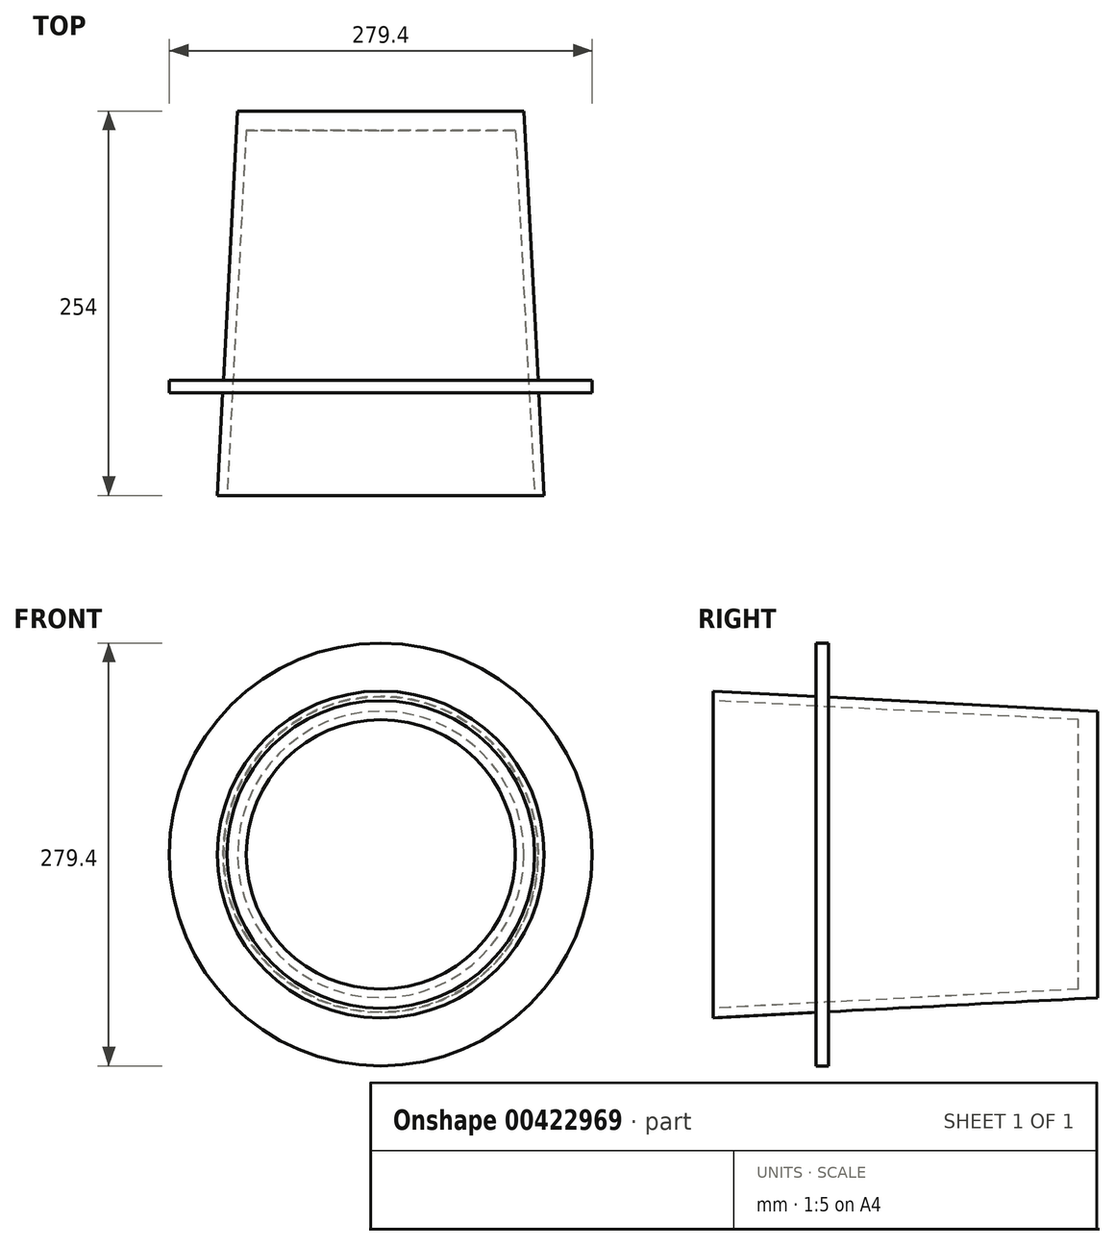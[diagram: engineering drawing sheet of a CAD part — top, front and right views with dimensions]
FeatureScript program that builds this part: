
annotation { "Feature Type Name" : "Feature", "Feature Type Description" : "" }
export const myFeature = defineFeature(function(context is Context, id is Id, definition is map)
    precondition{}
    {
        {
            var Q0;
            Q0=qCreatedBy(makeId("Front.planeOp"),FACE);
            var sketch = newSketch(context, id + "F0", { "sketchPlane" : qUnion([Q0])});
            skCircle(sketch, "E0", {"center": v(0, 0) * mm, "radius": 107.95 * mm});
            skSolve(sketch);
        }
        {
            var Q0;
            Q0 = qSketchRegion(id + "F0", true);
            extrude(context, id + "F1", {"entities" : qUnion([Q0]), "oppositeDirection" : true, "depth" : 254 * mm, "hasDraft" : true, "draftAngle" : 3 * degree, "draftPullDirection" : true});
        }
        {
            var Q0;
            Q0=makeQuery(id+"F1.opExtrude","CAP_FACE",FACE,{"disambiguationData":[OSD([sQuery(id+"F0.wireOp",EDGE,"E0")])],"isStart":true});
            var sketch = newSketch(context, id + "F2", { "sketchPlane" : qUnion([Q0])});
            skCircle(sketch, "E1", {"center": v(0, 0) * mm, "radius": 101.6 * mm});
            skSolve(sketch);
        }
        {
            var Q0;
            Q0 = qSketchRegion(id + "F2", true);
            extrude(context, id + "F3", {"entities" : qUnion([Q0]), "operationType" : NewBodyOperationType.REMOVE, "oppositeDirection" : true, "depth" : 241.3 * mm, "hasDraft" : true, "draftAngle" : 3 * degree, "draftPullDirection" : true});
        }
        {
            var Q0;
            Q0=makeQuery(id+"F1.opExtrude","CAP_FACE",FACE,{"disambiguationData":[OSD([sQuery(id+"F0.wireOp",EDGE,"E0")])],"isStart":true});
            cPlane(context, id + "F4", {"entities" : qUnion([Q0]), "cplaneType" : CPlaneType.OFFSET, "offset" : 76.2 * mm, "oppositeDirection" : true, "width" : 152.4 * mm, "height" : 152.4 * mm});
        }
        {
            var Q0;
            Q0=qCreatedBy(id+"F4.planeOp",FACE);
            var sketch = newSketch(context, id + "F5", { "sketchPlane" : qUnion([Q0])});
            skArc(sketch, "E2", {"start": v(-103.95, 0) * mm, "mid": v(-96.04, -39.78) * mm, "end": v(-73.5, -73.5) * mm});
            skArc(sketch, "E3", {"start": v(-139.7, 0) * mm, "mid": v(-129.07, -53.46) * mm, "end": v(-98.78, -98.78) * mm});
            skArc(sketch, "E4", {"start": v(-103.95, 0) * mm, "mid": v(-121.82, 17.88) * mm, "end": v(-139.7, 0) * mm});
            skArc(sketch, "E5", {"start": v(-98.78, -98.78) * mm, "mid": v(-73.5, -98.78) * mm, "end": v(-73.5, -73.5) * mm});
            skPoint(sketch, "E6.orphan", {"position": v(-98.78, -98.78) * mm});
            skPoint(sketch, "E7.start.orphan", {"position": v(-73.5, -73.5) * mm});
            skPoint(sketch, "E8.start.orphan", {"position": v(-96.04, -39.78) * mm});
            skArc(sketch, "E9.MirrorCS", {"start": v(73.5, 73.5) * mm, "mid": v(96.04, 39.78) * mm, "end": v(103.95, 0) * mm});
            skArc(sketch, "E10.MirrorCS", {"start": v(98.78, 98.78) * mm, "mid": v(129.07, 53.46) * mm, "end": v(139.7, 0) * mm});
            skArc(sketch, "E11.MirrorCS", {"start": v(73.5, 73.5) * mm, "mid": v(73.5, 98.78) * mm, "end": v(98.78, 98.78) * mm});
            skPoint(sketch, "E12.MirrorP", {"position": v(96.04, 39.78) * mm});
            skPoint(sketch, "E13.MirrorP", {"position": v(139.7, 0) * mm});
            skArc(sketch, "E14.MirrorCS", {"start": v(139.7, 0) * mm, "mid": v(121.82, -17.88) * mm, "end": v(103.95, 0) * mm});
            skPoint(sketch, "E15.MirrorP", {"position": v(103.95, 0) * mm});
            skSolve(sketch);
        }
        {
            var Q0;
            Q0=qCreatedBy(id+"F4.planeOp",FACE);
            var sketch = newSketch(context, id + "F6", { "sketchPlane" : qUnion([Q0])});
            skCircle(sketch, "E16", {"center": v(0, 0) * mm, "radius": 103.95 * mm});
            skCircle(sketch, "E17", {"center": v(0, 0) * mm, "radius": 139.7 * mm});
            skSolve(sketch);
        }
        {
            var Q0;
            Q0 = qSketchRegion(id + "F6", true);
            extrude(context, id + "F7", {"entities" : qUnion([Q0]), "operationType" : NewBodyOperationType.ADD, "depth" : 8.25 * mm});
        }
    });
